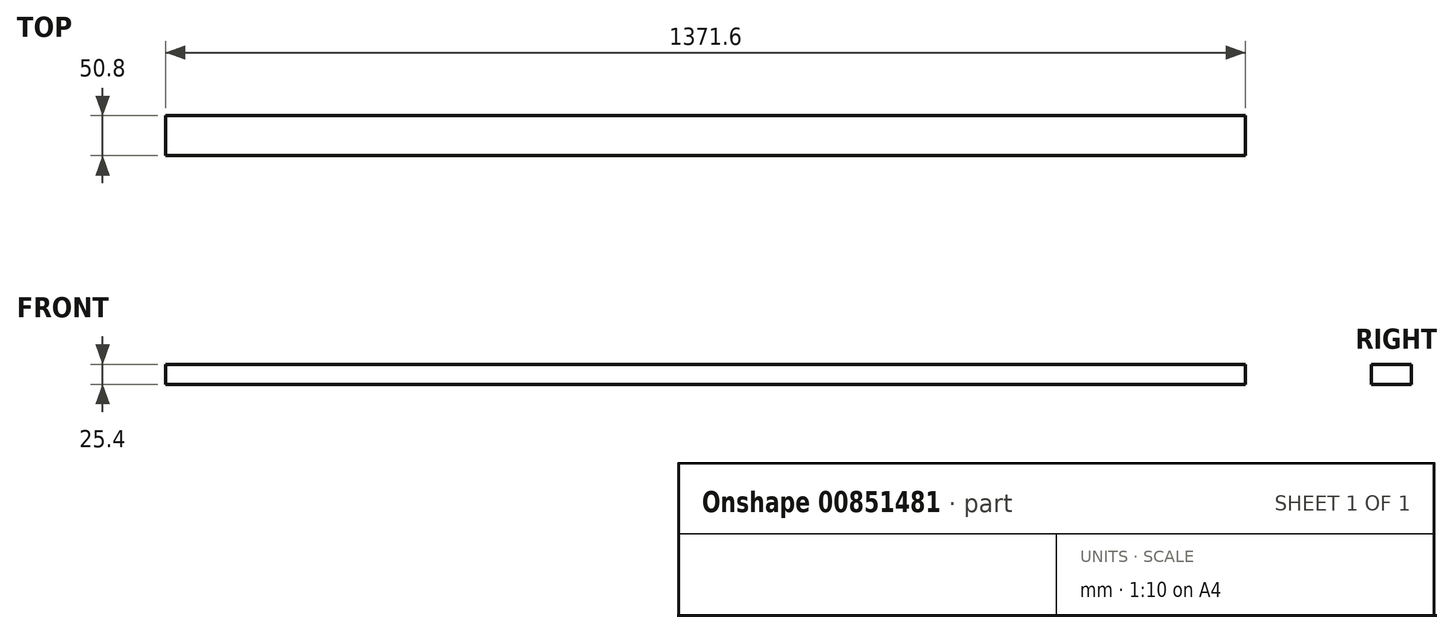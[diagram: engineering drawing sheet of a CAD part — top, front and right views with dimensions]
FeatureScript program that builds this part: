
annotation { "Feature Type Name" : "Feature", "Feature Type Description" : "" }
export const myFeature = defineFeature(function(context is Context, id is Id, definition is map)
    precondition{}
    {
        {
            var Q0;
            Q0=qCreatedBy(makeId("Front.planeOp"),FACE);
            var sketch = newSketch(context, id + "F0", { "sketchPlane" : qUnion([Q0])});
            skLineSegment(sketch, "E0.bottom", {"start": v(-37.42, 33.73) * mm, "end": v(1334.18, 33.73) * mm});
            skLineSegment(sketch, "E0.top", {"start": v(-37.42, 8.33) * mm, "end": v(1334.18, 8.33) * mm});
            skLineSegment(sketch, "E0.left", {"start": v(-37.42, 33.73) * mm, "end": v(-37.42, 8.33) * mm});
            skLineSegment(sketch, "E0.right", {"start": v(1334.18, 33.73) * mm, "end": v(1334.18, 8.33) * mm});
            skSolve(sketch);
        }
        {
            var Q0;
            Q0 = qSketchRegion(id + "F0", true);
            extrude(context, id + "F1", {"entities" : qUnion([Q0]), "depth" : 50.8 * mm, "offsetDistance" : 25 * mm});
        }
    });
